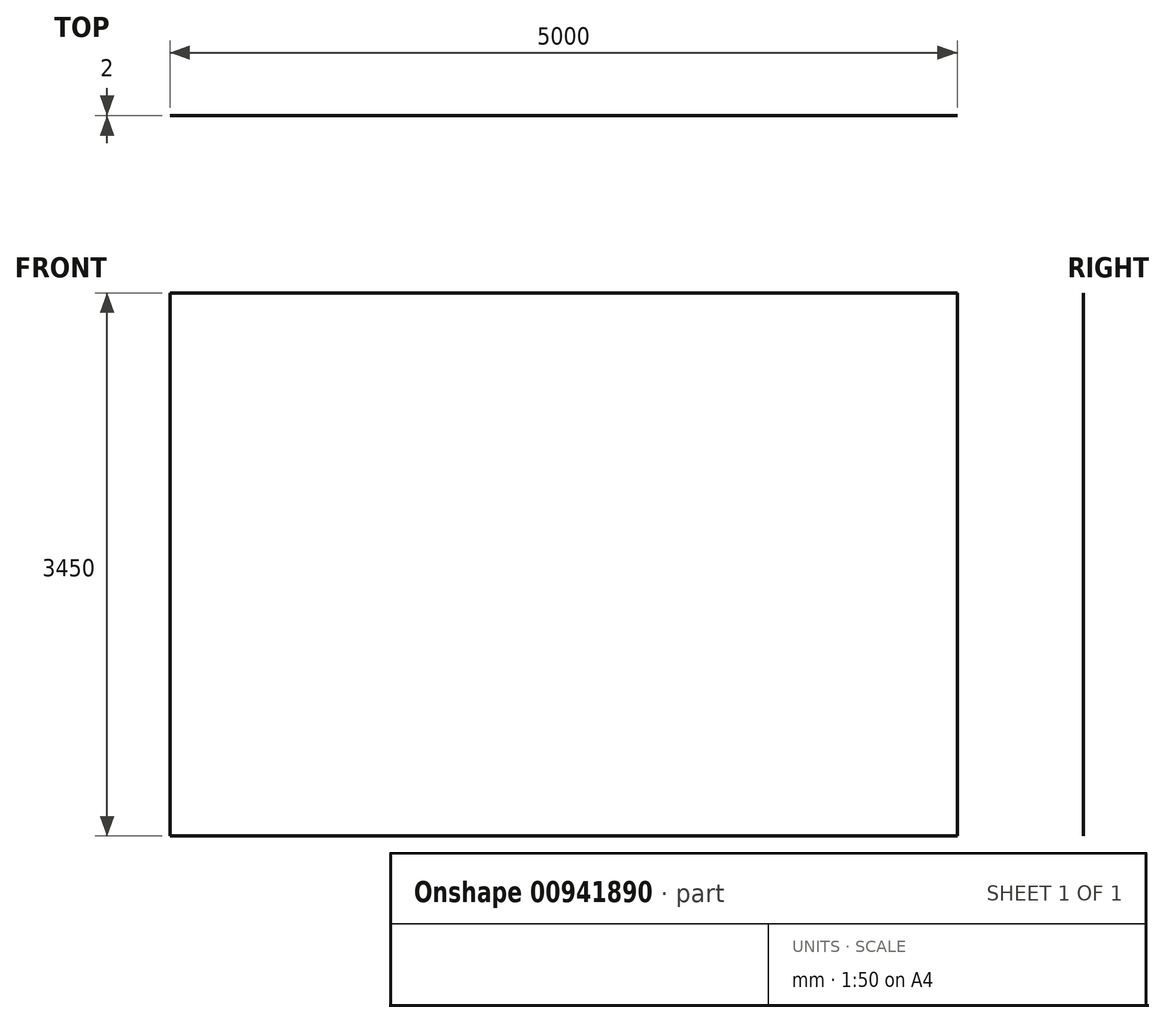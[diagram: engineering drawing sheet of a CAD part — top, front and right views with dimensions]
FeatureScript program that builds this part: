
annotation { "Feature Type Name" : "Feature", "Feature Type Description" : "" }
export const myFeature = defineFeature(function(context is Context, id is Id, definition is map)
    precondition{}
    {
        {
            var Q0;
            Q0=qCreatedBy(makeId("Front.planeOp"),FACE);
            var sketch = newSketch(context, id + "F0", { "sketchPlane" : qUnion([Q0])});
            skLineSegment(sketch, "E0.bottom", {"start": v(0, 0) * mm, "end": v(5000, 0) * mm});
            skLineSegment(sketch, "E0.top", {"start": v(0, 3450) * mm, "end": v(5000, 3450) * mm});
            skLineSegment(sketch, "E0.left", {"start": v(0, 0) * mm, "end": v(0, 3450) * mm});
            skLineSegment(sketch, "E0.right", {"start": v(5000, 0) * mm, "end": v(5000, 3450) * mm});
            skSolve(sketch);
        }
        {
            var Q0;
            Q0=makeQuery(id+"F0.imprint","IMPRINT",FACE,{"disambiguationData":[TD([[makeQuery(id+"F0.imprint","IMPRINT",EDGE,{"derivedFrom":sQuery(id+"F0.wireOp",EDGE,"E0.bottom")}),1.0]])]});
            extrude(context, id + "F1", {"entities" : qUnion([Q0]), "depth" : 2 * mm, "offsetDistance" : 25 * mm});
        }
    });
